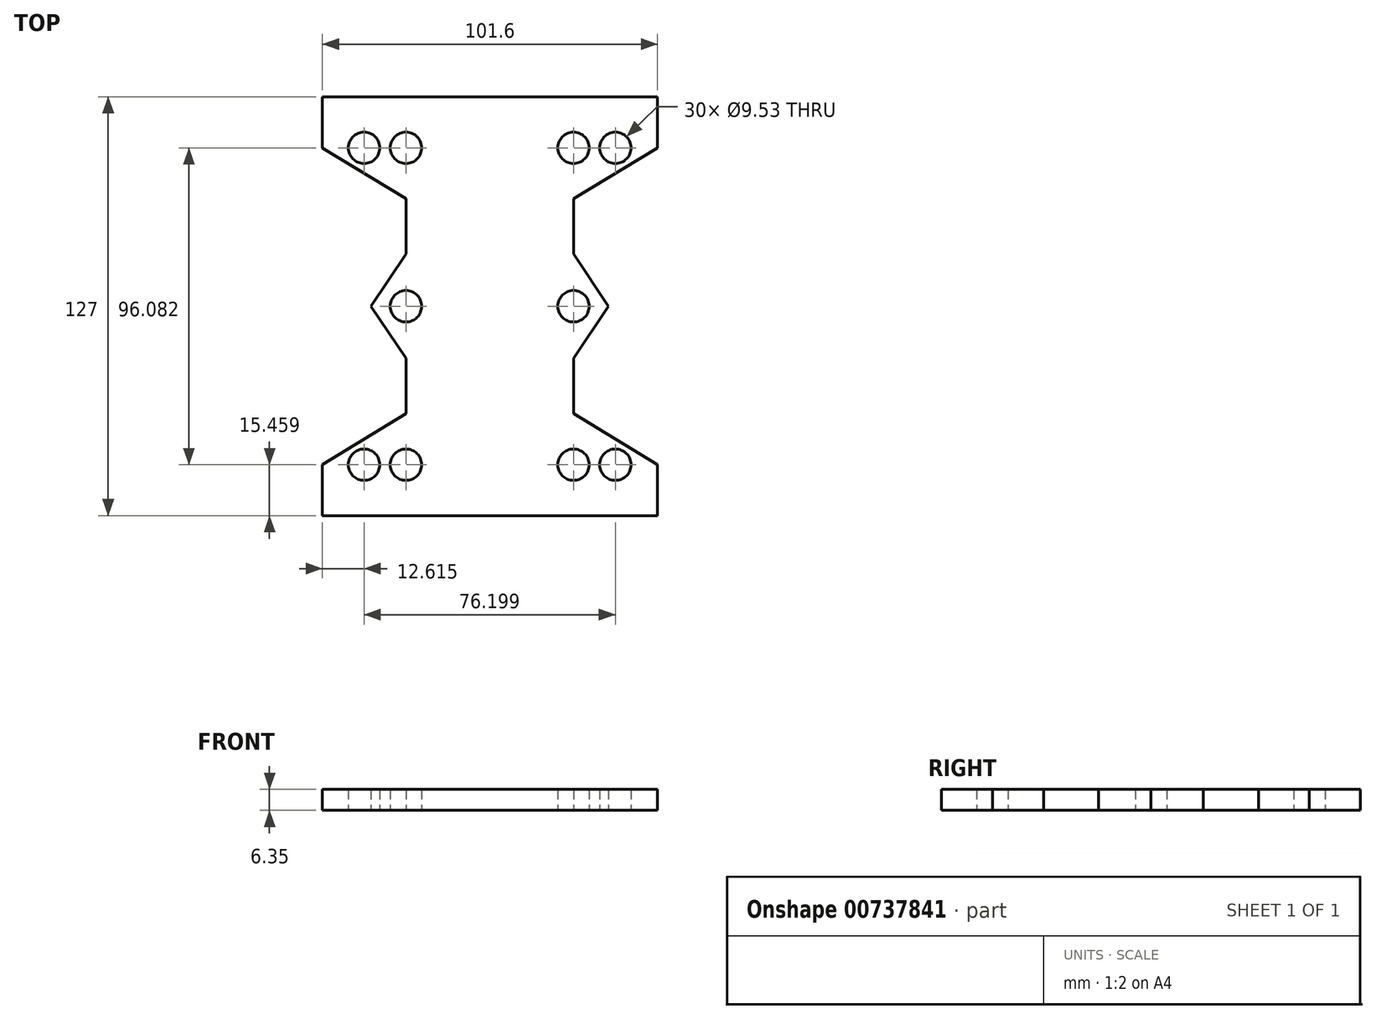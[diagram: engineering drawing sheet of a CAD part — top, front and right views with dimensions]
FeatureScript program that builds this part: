
annotation { "Feature Type Name" : "Feature", "Feature Type Description" : "" }
export const myFeature = defineFeature(function(context is Context, id is Id, definition is map)
    precondition{}
    {
        {
            var Q0;
            Q0=qCreatedBy(makeId("Top.planeOp"),FACE);
            var sketch = newSketch(context, id + "F0", { "sketchPlane" : qUnion([Q0])});
            skLineSegment(sketch, "E0.bottom", {"start": v(-50.13, 59.84) * mm, "end": v(51.47, 59.84) * mm});
            skLineSegment(sketch, "E0.top", {"start": v(-50.13, -67.16) * mm, "end": v(51.47, -67.16) * mm});
            skLineSegment(sketch, "E0.left", {"start": v(-50.13, 59.84) * mm, "end": v(-50.13, 44.38) * mm});
            skLineSegment(sketch, "E0.right", {"start": v(51.47, 59.84) * mm, "end": v(51.47, 44.38) * mm});
            skLineSegment(sketch, "E1.trimOffspring", {"start": v(-50.13, -51.7) * mm, "end": v(-50.13, -67.16) * mm});
            skLineSegment(sketch, "E2.trimOffspring", {"start": v(51.47, -51.7) * mm, "end": v(51.47, -67.16) * mm});
            skLineSegment(sketch, "E3", {"start": v(-24.81, 28.92) * mm, "end": v(-24.81, 12.17) * mm});
            skLineSegment(sketch, "E4", {"start": v(25.98, 28.92) * mm, "end": v(25.98, 12.17) * mm});
            skCircle(sketch, "E5", {"center": v(-24.81, 44.38) * mm, "radius": 4.76 * mm});
            skCircle(sketch, "E6", {"center": v(-24.81, -51.7) * mm, "radius": 4.76 * mm});
            skCircle(sketch, "E7", {"center": v(25.98, -51.7) * mm, "radius": 4.76 * mm});
            skCircle(sketch, "E8", {"center": v(25.98, 44.38) * mm, "radius": 4.76 * mm});
            skPoint(sketch, "E9.bottom.start.orphan", {"position": v(-24.81, -3.66) * mm});
            skLineSegment(sketch, "E10.trimOffspring", {"start": v(-24.81, -19.49) * mm, "end": v(-24.81, -36.24) * mm});
            skLineSegment(sketch, "E11.trimOffspring", {"start": v(25.98, -19.49) * mm, "end": v(25.98, -36.24) * mm});
            skCircle(sketch, "E12", {"center": v(-24.81, -3.66) * mm, "radius": 4.76 * mm});
            skCircle(sketch, "E13", {"center": v(25.98, -3.66) * mm, "radius": 4.76 * mm});
            skCircle(sketch, "E14.1.0.0", {"center": v(38.68, 44.38) * mm, "radius": 4.76 * mm});
            skLineSegment(sketch, "E14.direction1", {"start": v(25.98, 44.38) * mm, "end": v(38.68, 44.38) * mm, "construction": true});
            skCircle(sketch, "E15.1.0.0", {"center": v(38.68, -51.7) * mm, "radius": 4.76 * mm});
            skLineSegment(sketch, "E15.direction1", {"start": v(25.98, -51.7) * mm, "end": v(38.68, -51.7) * mm, "construction": true});
            skCircle(sketch, "E16.1.0.0", {"center": v(-37.51, 44.38) * mm, "radius": 4.76 * mm});
            skCircle(sketch, "E16.1.0.1", {"center": v(-37.51, -51.7) * mm, "radius": 4.76 * mm});
            skLineSegment(sketch, "E16.direction1", {"start": v(-24.81, -51.7) * mm, "end": v(-37.51, -51.7) * mm, "construction": true});
            skLineSegment(sketch, "E17", {"start": v(-24.81, 12.17) * mm, "end": v(-35.4, -3.66) * mm});
            skLineSegment(sketch, "E18", {"start": v(-35.4, -3.66) * mm, "end": v(-24.81, -19.49) * mm});
            skLineSegment(sketch, "E19", {"start": v(25.98, 12.17) * mm, "end": v(36.56, -3.66) * mm});
            skLineSegment(sketch, "E20", {"start": v(36.56, -3.66) * mm, "end": v(25.98, -19.49) * mm});
            skPoint(sketch, "E21.orphan", {"position": v(36.56, 12.17) * mm});
            skPoint(sketch, "E22.start.orphan", {"position": v(36.56, -19.49) * mm});
            skLineSegment(sketch, "E23", {"start": v(25.98, -36.24) * mm, "end": v(51.47, -51.7) * mm});
            skLineSegment(sketch, "E24", {"start": v(-24.81, -36.24) * mm, "end": v(-50.13, -51.7) * mm});
            skLineSegment(sketch, "E25", {"start": v(-24.81, 28.92) * mm, "end": v(-50.13, 44.38) * mm});
            skLineSegment(sketch, "E26", {"start": v(25.98, 28.92) * mm, "end": v(51.47, 44.38) * mm});
            skPoint(sketch, "E27.start.orphan", {"position": v(-50.13, 28.92) * mm});
            skPoint(sketch, "E28.MirrorCS.start.orphan", {"position": v(51.47, 28.92) * mm});
            skPoint(sketch, "E29.MirrorCS.start.orphan", {"position": v(-50.13, -36.24) * mm});
            skPoint(sketch, "E30.orphan", {"position": v(51.47, -36.24) * mm});
            skSolve(sketch);
        }
        {
            var Q0;
            Q0=makeQuery(id+"F0.imprint","IMPRINT",FACE,{"disambiguationData":[TD([[makeQuery(id+"F0.imprint","IMPRINT",EDGE,{"derivedFrom":sQuery(id+"F0.wireOp",EDGE,"E0.bottom")}),-1.0]])]});
            extrude(context, id + "F1", {"entities" : qUnion([Q0]), "depth" : 6.35 * mm, "offsetDistance" : 25 * mm});
        }
    });
